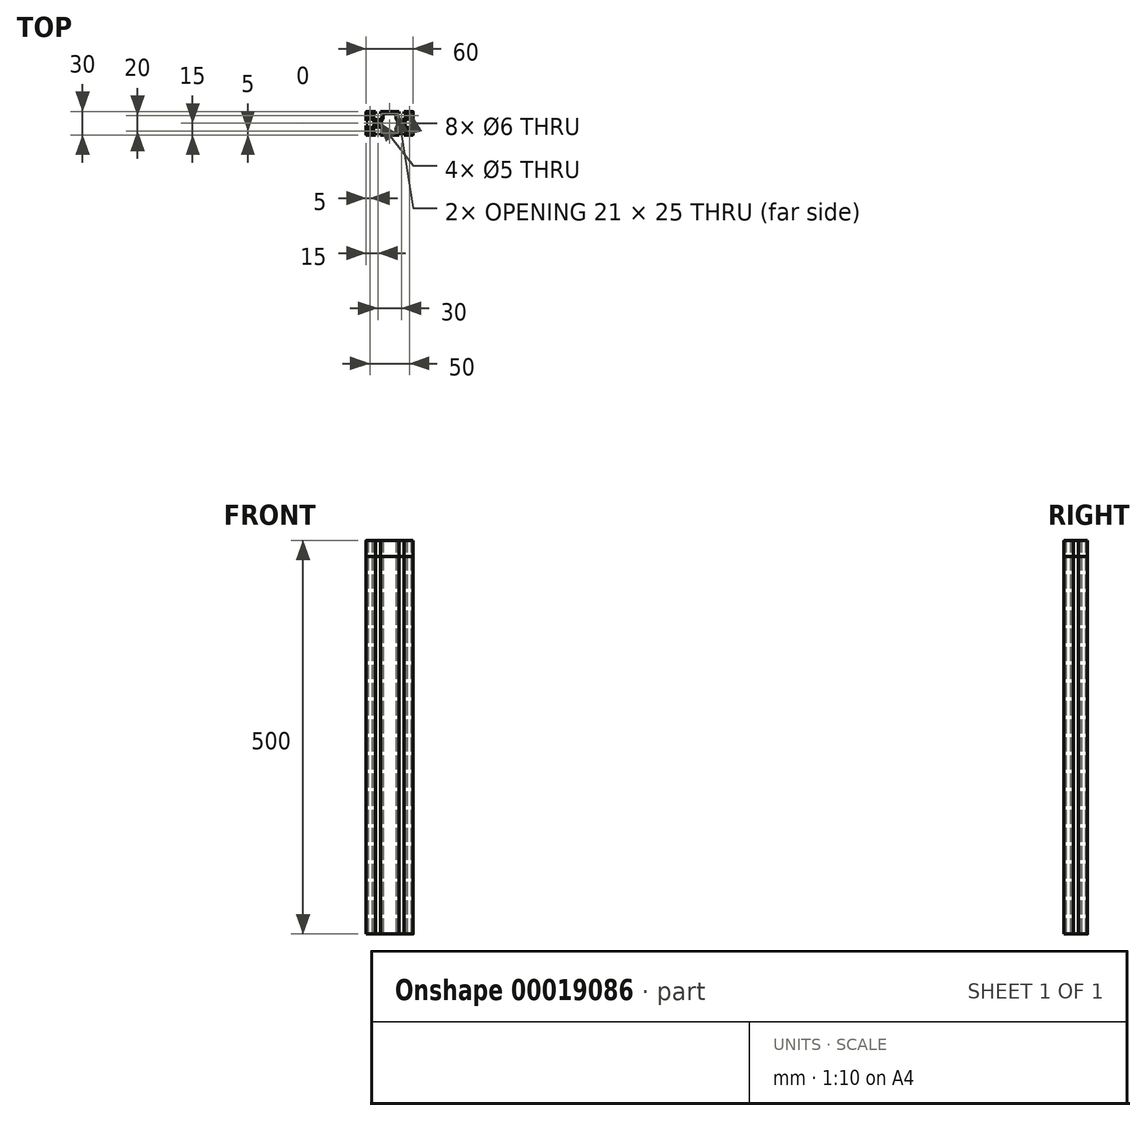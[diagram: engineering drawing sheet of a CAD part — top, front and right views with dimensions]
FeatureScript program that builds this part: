
annotation { "Feature Type Name" : "Feature", "Feature Type Description" : "" }
export const myFeature = defineFeature(function(context is Context, id is Id, definition is map)
    precondition{}
    {
        {
            var Q0;
            Q0=qCreatedBy(makeId("Top.planeOp"),FACE);
            var sketch = newSketch(context, id + "F0", { "sketchPlane" : qUnion([Q0])});
            skCircle(sketch, "E0", {"center": v(0, 0) * mm, "radius": 2.5 * mm});
            skLineSegment(sketch, "E1", {"start": v(0, 0) * mm, "end": v(-15, 0) * mm, "construction": true});
            skLineSegment(sketch, "E2", {"start": v(-15, 0) * mm, "end": v(-15, 15) * mm, "construction": true});
            skLineSegment(sketch, "E3", {"start": v(-15, 15) * mm, "end": v(0, 15) * mm, "construction": true});
            skLineSegment(sketch, "E4", {"start": v(0, 15) * mm, "end": v(0, 0) * mm, "construction": true});
            skLineSegment(sketch, "E5", {"start": v(-15, 15) * mm, "end": v(0, 0) * mm, "construction": true});
            skLineSegment(sketch, "E6", {"start": v(-15, 10) * mm, "end": v(-10, 10) * mm, "construction": true});
            skPoint(sketch, "E7", {"position": v(-15, 3.15) * mm});
            skPoint(sketch, "E8", {"position": v(-15, 5.5) * mm});
            skCircle(sketch, "E9", {"center": v(-10, 10) * mm, "radius": 3 * mm});
            skLineSegment(sketch, "E10", {"start": v(-15, 14.5) * mm, "end": v(-15, 3.15) * mm});
            skLineSegment(sketch, "E11", {"start": v(-15, 3.15) * mm, "end": v(-12.5, 3.15) * mm});
            skLineSegment(sketch, "E12", {"start": v(-12.5, 3.15) * mm, "end": v(-12.5, 5.5) * mm});
            skPoint(sketch, "E13", {"position": v(-4.5, 0) * mm});
            skLineSegment(sketch, "E14", {"start": v(-12.5, 5.5) * mm, "end": v(-5.5, 5.5) * mm, "construction": true});
            skArc(sketch, "E15", {"start": v(-4.5, 0) * mm, "mid": v(-5.13, 3) * mm, "end": v(-6.9, 5.5) * mm});
            skLineSegment(sketch, "E16", {"start": v(-12.5, 5.5) * mm, "end": v(-6.9, 5.5) * mm});
            skLineSegment(sketch, "E17.0.MirrorCS", {"start": v(-14.5, 15) * mm, "end": v(-3.15, 15) * mm});
            skPoint(sketch, "E18.visualSharp", {"position": v(-15, 15) * mm});
            skArc(sketch, "E18.filletArc", {"start": v(-14.5, 15) * mm, "mid": v(-14.85, 14.85) * mm, "end": v(-15, 14.5) * mm});
            skLineSegment(sketch, "E19.0.MirrorCS", {"start": v(-3.15, 15) * mm, "end": v(-3.15, 12.5) * mm});
            skLineSegment(sketch, "E20.0.MirrorCS", {"start": v(-3.15, 12.5) * mm, "end": v(-5.5, 12.5) * mm});
            skLineSegment(sketch, "E21.0.MirrorCS", {"start": v(-5.5, 12.5) * mm, "end": v(-5.5, 6.9) * mm});
            skArc(sketch, "E22.0.MirrorCS", {"start": v(0, 4.5) * mm, "mid": v(-3, 5.13) * mm, "end": v(-5.5, 6.9) * mm});
            skArc(sketch, "E23.0.MirrorCS", {"start": v(-4.5, 0) * mm, "mid": v(-5.13, -3) * mm, "end": v(-6.9, -5.5) * mm});
            skLineSegment(sketch, "E24.0.MirrorCS", {"start": v(-12.5, -5.5) * mm, "end": v(-6.9, -5.5) * mm});
            skLineSegment(sketch, "E25.0.MirrorCS", {"start": v(-12.5, -3.15) * mm, "end": v(-12.5, -5.5) * mm});
            skLineSegment(sketch, "E26.0.MirrorCS", {"start": v(-15, -3.15) * mm, "end": v(-12.5, -3.15) * mm});
            skLineSegment(sketch, "E27.0.MirrorCS", {"start": v(-15, -14.5) * mm, "end": v(-15, -3.15) * mm});
            skArc(sketch, "E28.0.MirrorCS", {"start": v(-14.5, -15) * mm, "mid": v(-14.85, -14.85) * mm, "end": v(-15, -14.5) * mm});
            skLineSegment(sketch, "E29.0.MirrorCS", {"start": v(-14.5, -15) * mm, "end": v(-3.15, -15) * mm});
            skLineSegment(sketch, "E30.0.MirrorCS", {"start": v(-3.15, -15) * mm, "end": v(-3.15, -12.5) * mm});
            skLineSegment(sketch, "E31.0.MirrorCS", {"start": v(-3.15, -12.5) * mm, "end": v(-5.5, -12.5) * mm});
            skLineSegment(sketch, "E32.0.MirrorCS", {"start": v(-5.5, -12.5) * mm, "end": v(-5.5, -6.9) * mm});
            skArc(sketch, "E33.0.MirrorCS", {"start": v(0, -4.5) * mm, "mid": v(-3, -5.13) * mm, "end": v(-5.5, -6.9) * mm});
            skCircle(sketch, "E34.0.MirrorC", {"center": v(-10, -10) * mm, "radius": 3 * mm});
            skArc(sketch, "E35.0.MirrorCS", {"start": v(0, 4.5) * mm, "mid": v(3, 5.13) * mm, "end": v(5.5, 6.9) * mm});
            skLineSegment(sketch, "E36.0.MirrorCS", {"start": v(5.5, 12.5) * mm, "end": v(5.5, 6.9) * mm});
            skLineSegment(sketch, "E37.0.MirrorCS", {"start": v(3.15, 12.5) * mm, "end": v(5.5, 12.5) * mm});
            skLineSegment(sketch, "E38.0.MirrorCS", {"start": v(3.15, 15) * mm, "end": v(3.15, 12.5) * mm});
            skArc(sketch, "E39.0.MirrorCS", {"start": v(0, -4.5) * mm, "mid": v(3, -5.13) * mm, "end": v(5.5, -6.9) * mm});
            skLineSegment(sketch, "E40.0.MirrorCS", {"start": v(5.5, -12.5) * mm, "end": v(5.5, -6.9) * mm});
            skLineSegment(sketch, "E41.0.MirrorCS", {"start": v(3.15, -12.5) * mm, "end": v(5.5, -12.5) * mm});
            skLineSegment(sketch, "E42.0.MirrorCS", {"start": v(3.15, -15) * mm, "end": v(3.15, -12.5) * mm});
            skLineSegment(sketch, "E43", {"start": v(0, 0) * mm, "end": v(30, 0) * mm, "construction": true});
            skPoint(sketch, "E44", {"position": v(15, 0) * mm});
            skLineSegment(sketch, "E45", {"start": v(15, 15) * mm, "end": v(15, -15) * mm, "construction": true});
            skCircle(sketch, "E46.0.MirrorC", {"center": v(30, 0) * mm, "radius": 2.5 * mm});
            skLineSegment(sketch, "E47.0.MirrorCS", {"start": v(26.85, 15) * mm, "end": v(26.85, 12.5) * mm});
            skLineSegment(sketch, "E48.0.MirrorCS", {"start": v(26.85, 12.5) * mm, "end": v(24.5, 12.5) * mm});
            skLineSegment(sketch, "E49.0.MirrorCS", {"start": v(24.5, 12.5) * mm, "end": v(24.5, 6.9) * mm});
            skArc(sketch, "E50.0.MirrorCS", {"start": v(30, 4.5) * mm, "mid": v(27, 5.13) * mm, "end": v(24.5, 6.9) * mm});
            skArc(sketch, "E51.0.MirrorCS", {"start": v(30, 4.5) * mm, "mid": v(33, 5.13) * mm, "end": v(35.5, 6.9) * mm});
            skLineSegment(sketch, "E52.0.MirrorCS", {"start": v(35.5, 12.5) * mm, "end": v(35.5, 6.9) * mm});
            skLineSegment(sketch, "E53.0.MirrorCS", {"start": v(33.15, 12.5) * mm, "end": v(35.5, 12.5) * mm});
            skLineSegment(sketch, "E54.0.MirrorCS", {"start": v(33.15, 15) * mm, "end": v(33.15, 12.5) * mm});
            skLineSegment(sketch, "E55.0.MirrorCS", {"start": v(44.5, 15) * mm, "end": v(33.15, 15) * mm});
            skArc(sketch, "E56.0.MirrorCS", {"start": v(44.5, 15) * mm, "mid": v(44.85, 14.85) * mm, "end": v(45, 14.5) * mm});
            skLineSegment(sketch, "E57.0.MirrorCS", {"start": v(45, 14.5) * mm, "end": v(45, 3.15) * mm});
            skLineSegment(sketch, "E58.0.MirrorCS", {"start": v(45, 3.15) * mm, "end": v(42.5, 3.15) * mm});
            skLineSegment(sketch, "E59.0.MirrorCS", {"start": v(42.5, 3.15) * mm, "end": v(42.5, 5.5) * mm});
            skLineSegment(sketch, "E60.0.MirrorCS", {"start": v(42.5, 5.5) * mm, "end": v(36.9, 5.5) * mm});
            skArc(sketch, "E61.0.MirrorCS", {"start": v(34.5, 0) * mm, "mid": v(35.13, 3) * mm, "end": v(36.9, 5.5) * mm});
            skArc(sketch, "E62.0.MirrorCS", {"start": v(34.5, 0) * mm, "mid": v(35.13, -3) * mm, "end": v(36.9, -5.5) * mm});
            skLineSegment(sketch, "E63.0.MirrorCS", {"start": v(42.5, -5.5) * mm, "end": v(36.9, -5.5) * mm});
            skLineSegment(sketch, "E64.0.MirrorCS", {"start": v(42.5, -3.15) * mm, "end": v(42.5, -5.5) * mm});
            skLineSegment(sketch, "E65.0.MirrorCS", {"start": v(45, -3.15) * mm, "end": v(42.5, -3.15) * mm});
            skLineSegment(sketch, "E66.0.MirrorCS", {"start": v(45, -14.5) * mm, "end": v(45, -3.15) * mm});
            skArc(sketch, "E67.0.MirrorCS", {"start": v(44.5, -15) * mm, "mid": v(44.85, -14.85) * mm, "end": v(45, -14.5) * mm});
            skLineSegment(sketch, "E68.0.MirrorCS", {"start": v(44.5, -15) * mm, "end": v(33.15, -15) * mm});
            skLineSegment(sketch, "E69.0.MirrorCS", {"start": v(33.15, -15) * mm, "end": v(33.15, -12.5) * mm});
            skLineSegment(sketch, "E70.0.MirrorCS", {"start": v(33.15, -12.5) * mm, "end": v(35.5, -12.5) * mm});
            skLineSegment(sketch, "E71.0.MirrorCS", {"start": v(35.5, -12.5) * mm, "end": v(35.5, -6.9) * mm});
            skArc(sketch, "E72.0.MirrorCS", {"start": v(30, -4.5) * mm, "mid": v(33, -5.13) * mm, "end": v(35.5, -6.9) * mm});
            skArc(sketch, "E73.0.MirrorCS", {"start": v(30, -4.5) * mm, "mid": v(27, -5.13) * mm, "end": v(24.5, -6.9) * mm});
            skLineSegment(sketch, "E74.0.MirrorCS", {"start": v(24.5, -12.5) * mm, "end": v(24.5, -6.9) * mm});
            skLineSegment(sketch, "E75.0.MirrorCS", {"start": v(26.85, -12.5) * mm, "end": v(24.5, -12.5) * mm});
            skLineSegment(sketch, "E76.0.MirrorCS", {"start": v(26.85, -15) * mm, "end": v(26.85, -12.5) * mm});
            skCircle(sketch, "E77.0.MirrorC", {"center": v(40, -10) * mm, "radius": 3 * mm});
            skCircle(sketch, "E78.0.MirrorC", {"center": v(40, 10) * mm, "radius": 3 * mm});
            skLineSegment(sketch, "E79", {"start": v(3.15, 15) * mm, "end": v(26.85, 15) * mm});
            skLineSegment(sketch, "E80", {"start": v(3.15, -15) * mm, "end": v(26.85, -15) * mm});
            skLineSegment(sketch, "E81.0.MirrorCS", {"start": v(0, 15) * mm, "end": v(0, 30) * mm, "construction": true});
            skArc(sketch, "E82.0.MirrorCS", {"start": v(4.5, 0) * mm, "mid": v(5.05, 2.82) * mm, "end": v(6.62, 5.22) * mm});
            skLineSegment(sketch, "E83", {"start": v(6.9, 5.92) * mm, "end": v(6.9, 11.5) * mm});
            skLineSegment(sketch, "E84", {"start": v(7.9, 12.5) * mm, "end": v(15, 12.5) * mm});
            skPoint(sketch, "E85.visualSharp", {"position": v(6.9, 5.5) * mm});
            skArc(sketch, "E85.filletArc", {"start": v(6.62, 5.22) * mm, "mid": v(6.83, 5.54) * mm, "end": v(6.9, 5.92) * mm});
            skPoint(sketch, "E86.visualSharp", {"position": v(6.9, 12.5) * mm});
            skArc(sketch, "E86.filletArc", {"start": v(7.9, 12.5) * mm, "mid": v(7.2, 12.2) * mm, "end": v(6.9, 11.5) * mm});
            skPoint(sketch, "E87", {"position": v(15, 12.5) * mm});
            skLineSegment(sketch, "E88.0.MirrorCS", {"start": v(22.1, 12.5) * mm, "end": v(15, 12.5) * mm});
            skArc(sketch, "E89.0.MirrorCS", {"start": v(22.1, 12.5) * mm, "mid": v(22.8, 12.2) * mm, "end": v(23.1, 11.5) * mm});
            skLineSegment(sketch, "E90.0.MirrorCS", {"start": v(23.1, 5.92) * mm, "end": v(23.1, 11.5) * mm});
            skArc(sketch, "E91.0.MirrorCS", {"start": v(23.38, 5.22) * mm, "mid": v(23.17, 5.54) * mm, "end": v(23.1, 5.92) * mm});
            skArc(sketch, "E92.0.MirrorCS", {"start": v(25.5, 0) * mm, "mid": v(24.95, 2.82) * mm, "end": v(23.38, 5.22) * mm});
            skArc(sketch, "E93.0.MirrorCS", {"start": v(4.5, 0) * mm, "mid": v(5.05, -2.82) * mm, "end": v(6.62, -5.22) * mm});
            skPoint(sketch, "E94.0.MirrorP", {"position": v(6.9, -5.5) * mm});
            skArc(sketch, "E95.0.MirrorCS", {"start": v(6.62, -5.22) * mm, "mid": v(6.83, -5.54) * mm, "end": v(6.9, -5.92) * mm});
            skLineSegment(sketch, "E96.0.MirrorCS", {"start": v(6.9, -5.92) * mm, "end": v(6.9, -11.5) * mm});
            skLineSegment(sketch, "E97.0.MirrorCS", {"start": v(7.9, -12.5) * mm, "end": v(15, -12.5) * mm});
            skArc(sketch, "E98.0.MirrorCS", {"start": v(7.9, -12.5) * mm, "mid": v(7.2, -12.2) * mm, "end": v(6.9, -11.5) * mm});
            skLineSegment(sketch, "E99.0.MirrorCS", {"start": v(22.1, -12.5) * mm, "end": v(15, -12.5) * mm});
            skArc(sketch, "E100.0.MirrorCS", {"start": v(22.1, -12.5) * mm, "mid": v(22.8, -12.2) * mm, "end": v(23.1, -11.5) * mm});
            skLineSegment(sketch, "E101.0.MirrorCS", {"start": v(23.1, -5.92) * mm, "end": v(23.1, -11.5) * mm});
            skArc(sketch, "E102.0.MirrorCS", {"start": v(23.38, -5.22) * mm, "mid": v(23.17, -5.54) * mm, "end": v(23.1, -5.92) * mm});
            skArc(sketch, "E103.0.MirrorCS", {"start": v(25.5, 0) * mm, "mid": v(24.95, -2.82) * mm, "end": v(23.38, -5.22) * mm});
            skSolve(sketch);
        }
        {
            var Q0;
            Q0=qSketchRegion(id+"F0",true);
            extrude(context, id + "F1", {"entities" : qUnion([Q0]), "depth" : 500 * mm});
        }
        {
            var Q0;
            Q0=qSketchRegion(id+"F0",true);
            extrude(context, id + "F2", {"entities" : qUnion([Q0]), "depth" : 480 * mm});
        }
    });
